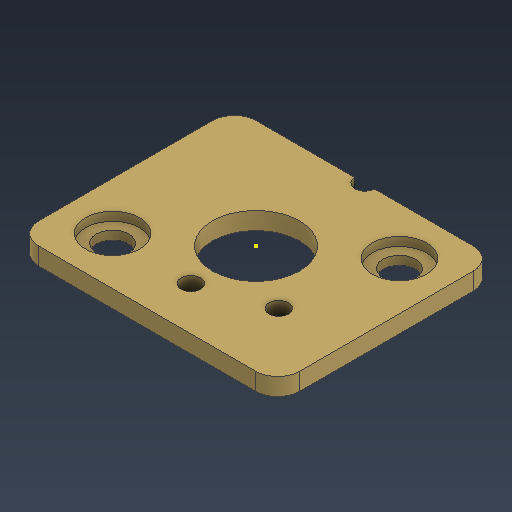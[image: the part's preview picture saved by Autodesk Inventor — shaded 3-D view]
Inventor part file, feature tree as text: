
AUTODESK INVENTOR PART (.ipt)
format: ipt  version: 2021 (Build 250183000, 183)  size: 165,888 bytes
history: native  units: mm
features: extrude x4, sketch x2, other x1
ambient origin geometry x8: Origin, YZ Plane, XZ Plane, XY Plane, X Axis, Y Axis, Z Axis, Center Point
bodies: Body1 (feature_tree)
feature tree (7):
  other  "Chapa Inferior"
  sketch  "Esboço2"  dims[d16=0.9mm d17=1.5mm]
  extrude  "Extrusão3"  Depth=1.5mm
  extrude  "Extrusão4"  Depth=0.8mm TaperAngle=0.0deg
  extrude  "Extrusão5"  Depth=0.4mm TaperAngle=0.0deg
  extrude  "Extrusão6"  Depth=10.0mm
  sketch  "Esboço4"  dims[d18=1.5mm d19=0.8mm d20=0.0mm d21=0.4mm d22=0.0mm d23=4.0mm d24=10.0mm d25=0.0mm d26=2.0mm d27=0.0mm d28=10.0mm d29=0.0mm d12=0.5mm d13=0.872665mm d14=0.5mm d15=0.872665mm]
